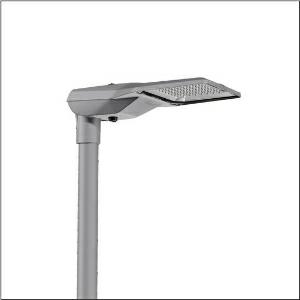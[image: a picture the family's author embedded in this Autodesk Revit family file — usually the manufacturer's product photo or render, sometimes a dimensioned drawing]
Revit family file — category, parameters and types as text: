
# Revit family: streetlight_sl_21_iq_midi___stw1_0a_5xe3e31y08nb_e460
name_source: partatom
category: Lighting Fixtures
units: mm (PartAtom-declared; Revit-internal decimal feet)

## family parameters
Cut with Voids When Loaded = No
Host = Face
Light Source = No
Part Type = Normal
Room Calculation Point = No
Round Connector Dimension = Use Diameter
Shared = No

## types (1)
- --- (1 x LED, 21550 lm, 136.6 W, 3000K)
    Apparent Load = 137 VA
    CIE Flux Codes = 39 75 98 100 100
    Color Rendering = 70
    Color Temperature = 3000K
    Default Elevation = 1800 mm
    Description = Streetlight SL 21 iQ midi, mast luminaire, primary light control with lens, of PMMA, primary optical cover: cover, of toughened safety glass, transparent, light distribution: STW1.0a, light emission: direct distribution, primary light characteristic: asymmetric, installation type: post-top, side-entry, LED, High Power LED, rated luminous flux: 21.550lm, luminous efficacy: 158lm/W, light colour: 730, colour temperature: 3000K, control gear: iQ-Street Remote, D4i with power reduction, control: pre-setting: logarithmic dimming characteristic, Street-Remote, Auto-Match, Temp-Guard, Lumen-Switch, Night-Set, Smart-Wire, Light-Fading, Desk-Remote (wireless, voltage-free reading and setting of iQ features in the workshop via application-optimized NFC function/RFID function), optimised constant luminous flux control (CLO 2.0), mains connection: 230..240V, AC, 50/60Hz, start of lifetime: 137W, end of service life: 144W, reduction: 61W, luminaire housing, of diecast aluminium, powder-coated, Siteco® metallic grey (DB 702S), corrosivity category C5 mid according to DIN EN ISO 12944, please order mast flange separately, inclination adjustable: 0°, 5°, 10°, 15°, sealing non-destructively replaceable, multi-level sealing system, length: 644mm, width: 335mm, height: 110mm, mast flange for spigot size: 42mm (side-entry): 5XC10008XM4, 60/48mm (side-entry/post-top): 5XC10108XM2, 76/60mm (side-entry/post-top): 5XC10108XM1, mounting height: 4..8m, Smart Interface below and above, protection rating (complete): IP66, insulation class (complete): insulation class II (safety insulation), certification: CE, ENEC, ENEC+, VDE, impact resistance: IK10, permissible operating ambient temperature for outdoor applications: -40..+50°C, standard-compliant lighting for roads and squares, packaging unit: 1 piece

Light Distribution: STW1.0a
    Height = 111 mm
    Lamp = 1 x LED
    Lamp Light Flux = 21550 lm
    Lamp Power = 136.6 W
    Lamp count = 1
    Length = 644 mm
    Luminous efficacy = 158 lm/W
    Manufacturer = Siteco
    ModVariant = No
    Model = 5XE3E31Y08NB
    Number of Poles = 1
    OnlyDefault = Yes
    Power Factor = 1
    Product Name = Streetlight SL 21 iQ midi | STW1.0a
    Product group = mast luminaire | pylon top
    ProductGroupID = 6100
    Protection Class = Protection class II
    Protection Degree = IP 66
    RLX_Detail_Level = 1
    RLX_Emergency_Light_Flux = 0 lm
    RLX_Emergency_Type = 0
    RLX_Emergency_Type_DB = No
    RlxData = <blob elided: 27357 chars, md5=5f56e7e7>
    Socket = socket
    Standby Power = 0 W
    System Light Flux = 21550 lm
    System Power = 137 W
    Type Comments = factory setting: luminous flux: 100 % | dim-lin: 254 | 733 mA
    Type Image = l_1004304.jpg
    URL = http://relux.com
    VarID = @adj_113654
    Voltage = 0 V
    Weight = 0.00 kg
    Width = 336 mm

## geometry (parser evidence)
native form markers: Blend x4, Sweep x10
no freeform markers — native parametric forms only
